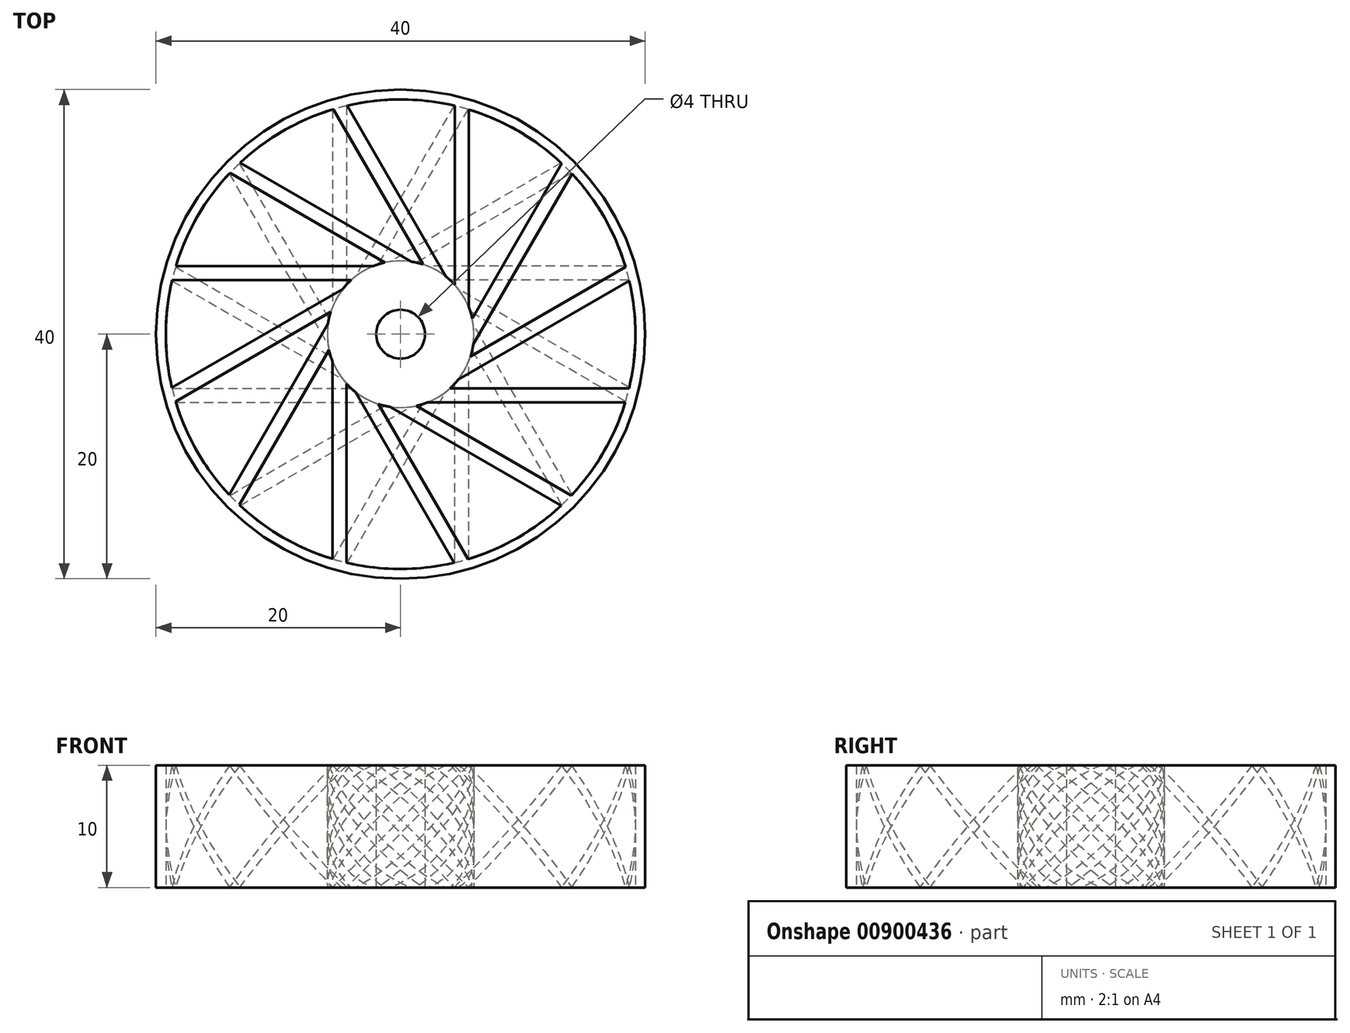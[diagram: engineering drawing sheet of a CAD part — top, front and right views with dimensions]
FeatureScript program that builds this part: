
annotation { "Feature Type Name" : "Feature", "Feature Type Description" : "" }
export const myFeature = defineFeature(function(context is Context, id is Id, definition is map)
    precondition{}
    {
        {
            var Q0;
            Q0=qCreatedBy(makeId("Top.planeOp"),FACE);
            var sketch = newSketch(context, id + "F0", { "sketchPlane" : qUnion([Q0])});
            skCircle(sketch, "E0", {"center": v(0, 0) * mm, "radius": 2 * mm});
            skCircle(sketch, "E1", {"center": v(0, 0) * mm, "radius": 20 * mm});
            skCircle(sketch, "E2", {"center": v(0, 0) * mm, "radius": 6 * mm});
            skCircle(sketch, "E3", {"center": v(0, 0) * mm, "radius": 19.2 * mm});
            skSolve(sketch);
        }
        {
            var Q0;
            Q0 = qSketchRegion(id + "F0", true);
            var Q1;
            Q1=makeQuery(id+"F0.imprint","IMPRINT",FACE,{"disambiguationData":[TD([[makeQuery(id+"F0.imprint","IMPRINT",EDGE,{"derivedFrom":sQuery(id+"F0.wireOp",EDGE,"E0")}),-1.0]])]});
            extrude(context, id + "F1", {"entities" : qUnion([Q0, Q1]), "depth" : 10 * mm, "offsetDistance" : 25 * mm});
        }
        {
            var Q0;
            Q0=qCreatedBy(makeId("Right.planeOp"),FACE);
            var sketch = newSketch(context, id + "F2", { "sketchPlane" : qUnion([Q0])});
            skLineSegment(sketch, "E4", {"start": v(0, 5) * mm, "end": v(5, 0) * mm, "construction": true});
            skLineSegment(sketch, "E5", {"start": v(0, 0) * mm, "end": v(0, 10) * mm, "construction": true});
            skLineSegment(sketch, "E6", {"start": v(-5, 10) * mm, "end": v(0, 5) * mm, "construction": true});
            skLineSegment(sketch, "E7.0", {"start": v(-5.57, 10) * mm, "end": v(4.43, 0) * mm});
            skLineSegment(sketch, "E8.0", {"start": v(-4.43, 10) * mm, "end": v(5.57, 0) * mm});
            skLineSegment(sketch, "E9", {"start": v(-5.57, 10) * mm, "end": v(-4.43, 10) * mm});
            skLineSegment(sketch, "E10", {"start": v(4.43, 0) * mm, "end": v(5.57, 0) * mm});
            skSolve(sketch);
        }
        {
            var Q0;
            Q0=makeQuery(id+"F2.imprint","IMPRINT",FACE,{"disambiguationData":[TD([[makeQuery(id+"F2.imprint","IMPRINT",EDGE,{"derivedFrom":sQuery(id+"F2.wireOp",EDGE,"E7.0")}),1.0]])]});
            extrude(context, id + "F3", {"entities" : qUnion([Q0]), "depth" : 20 * mm, "offsetDistance" : 25 * mm, "hasSecondDirection" : true, "secondDirectionOppositeDirection" : false, "secondDirectionDepth" : 2 * mm});
        }
        {
            var Q0;
            Q0=makeQuery(id+"F0.imprint","IMPRINT",FACE,{"disambiguationData":[TD([[makeQuery(id+"F0.imprint","IMPRINT",EDGE,{"derivedFrom":sQuery(id+"F0.wireOp",EDGE,"E0")}),-1.0]])]});
            var Q1;
            Q1=makeQuery(id+"F0.imprint","IMPRINT",FACE,{"disambiguationData":[TD([[makeQuery(id+"F0.imprint","IMPRINT",EDGE,{"derivedFrom":sQuery(id+"F0.wireOp",EDGE,"E2")}),-1.0]])]});
            var Q2;
            Q2=makeQuery(id+"F0.imprint","IMPRINT",FACE,{"disambiguationData":[TD([[makeQuery(id+"F0.imprint","IMPRINT",EDGE,{"derivedFrom":sQuery(id+"F0.wireOp",EDGE,"E1")}),1.0]])]});
            extrude(context, id + "F4", {"entities" : qUnion([Q0, Q1, Q2]), "depth" : 25 * mm, "offsetDistance" : 25 * mm});
        }
        {
            var Q0;
            Q0=makeQuery(id+"F4.opExtrude","SWEPT_BODY",BODY,{"disambiguationData":[OSD([sQuery(id+"F0.wireOp",EDGE,"E0"),sQuery(id+"F0.wireOp",EDGE,"E1")])]});
            var Q1;
            Q1=makeQuery(id+"F3.opExtrude","SWEPT_BODY",BODY,{"disambiguationData":[OSD([sQuery(id+"F2.wireOp",EDGE,"E7.0"),sQuery(id+"F2.wireOp",EDGE,"E8.0"),sQuery(id+"F2.wireOp",EDGE,"E9"),sQuery(id+"F2.wireOp",EDGE,"E10")])]});
            booleanBodies(context, id + "F5", {"operationType" : BooleanOperationType.INTERSECTION, "tools" : qUnion([Q0, Q1])});
        }
        {
            var Q0;
            Q0=makeQuery(id+"F5.opBoolean","INTERSECT",BODY,{"derivedFrom":[makeQuery(id+"F3.opExtrude","SWEPT_BODY",BODY,{"disambiguationData":[OSD([sQuery(id+"F2.wireOp",EDGE,"E7.0"),sQuery(id+"F2.wireOp",EDGE,"E8.0"),sQuery(id+"F2.wireOp",EDGE,"E9"),sQuery(id+"F2.wireOp",EDGE,"E10")])]}),makeQuery(id+"F4.opExtrude","SWEPT_BODY",BODY,{"disambiguationData":[OSD([sQuery(id+"F0.wireOp",EDGE,"E0"),sQuery(id+"F0.wireOp",EDGE,"E1")])]})]});
            var Q1;
            Q1=sQuery(id+"F2.wireOp",EDGE,"E5");
            circularPattern(context, id + "F6", {"operationType" : NewBodyOperationType.ADD, "entities" : qUnion([Q0]), "axis" : qUnion([Q1]), "angle" : 360 * degree, "instanceCount" : 12, "equalSpace" : true});
        }
    });
